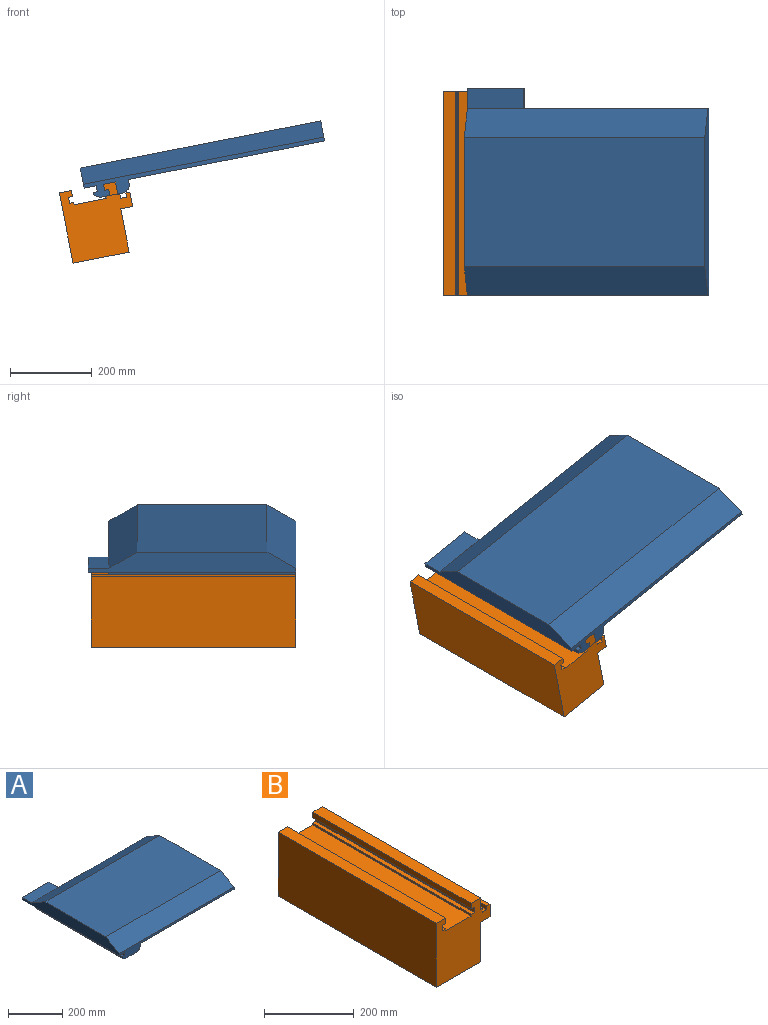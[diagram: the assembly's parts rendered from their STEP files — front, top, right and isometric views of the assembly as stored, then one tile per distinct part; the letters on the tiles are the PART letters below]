
ASSEMBLY  parts=2 mates=1
PART A: 19 faces, bbox 600x507.2x80 mm
  f0: plane 90x30mm, normal (0,1,0), area 2411.7mm2, adj f3,f4,f5,f6,f7,f8,f14,f15
  f1: plane 600x317.2mm, normal (0,0,1), area 190320mm2, adj f2,f9,f12,f13
  f2: plane 507.2x50mm, normal (-1,0,0), area 20505.5mm2, adj f1,f8,f10,f11,f12,f13,f16,f18
  f3: plane 457.2x15mm, normal (-1,0,0), area 6858mm2, adj f0,f4,f8,f10
  f4: plane 457.2x10mm, normal (0,0,1), area 4572mm2, adj f0,f3,f5,f10
  f5: plane 457.2x8.01mm, normal (-1,0,0), area 3660.1mm2, adj f0,f4,f10,f15
  f6: plane 457.2x55mm, normal (0,0,-1), area 25146mm2, adj f0,f10,f14,f15
  f7: plane 457.2x10mm, normal (1,0,0), area 4572mm2, adj f0,f8,f10,f14
  f8: plane 600x507.2mm, normal (0,0,-1), area 244744mm2, adj f0,f2,f3,f7,f9,f10,f11,f17
  f9: plane 457.2x50mm, normal (1,0,0), area 20031mm2, adj f1,f8,f10,f11,f12,f13
  f10: plane 600x39.59mm, normal (0,-1,0), area 8163mm2, adj f2,f3,f4,f5,f6,f7,f8,f9
  f11: plane 600x9.59mm, normal (0,1,0), area 4422.7mm2, adj f2,f8,f9,f13,f16,f17
  f12: plane 600x70mm, normal (0,-0.5,0.87), area 48497.4mm2, adj f1,f2,f9,f10
  f13: plane 600x70mm, normal (0,0.5,0.87), area 48497.4mm2, adj f1,f2,f9,f11
  f14: cylinder r=20mm len=457.2mm, axis (0,1,0), area 14363.4mm2, adj f0,f6,f7,f10
  f15: plane 457.2x15mm, normal (-0.42,0,-0.91), area 7567mm2, adj f0,f5,f6,f10
  f16: plane 140x50mm, normal (0,0,1), area 7000mm2, adj f2,f11,f17,f18
  f17: plane 50x9.49mm, normal (1,0,0), area 474.5mm2, adj f8,f11,f16,f18
  f18: plane 140x9.49mm, normal (0,1,0), area 1328.6mm2, adj f2,f8,f16,f17
PART B: 26 faces, bbox 170x500x175 mm
  f0: plane 500x30mm, normal (0,0,1), area 15000mm2, adj f1,f23,f24,f25
  f1: plane 500x175mm, normal (-1,0,0), area 87500mm2, adj f0,f2,f24,f25
  f2: plane 500x140mm, normal (0,0,-1), area 70000mm2, adj f1,f3,f24,f25
  f3: plane 500x108mm, normal (1,0,0), area 54000mm2, adj f2,f4,f24,f25
  f4: plane 500x30mm, normal (0,0,-1), area 15000mm2, adj f3,f5,f24,f25
  f5: plane 500x35mm, normal (1,0,0), area 17500mm2, adj f4,f6,f24,f25
  f6: plane 500x10mm, normal (0,0,1), area 5000mm2, adj f5,f7,f24,f25
  f7: plane 500x10mm, normal (-1,0,0), area 5000mm2, adj f6,f8,f24,f25
  f8: plane 500x15mm, normal (0,0,1), area 7500mm2, adj f7,f9,f24,f25
  f9: plane 500x10mm, normal (1,0,0), area 5000mm2, adj f8,f10,f24,f25
  f10: plane 500x5mm, normal (0,0,1), area 2500mm2, adj f9,f11,f24,f25
  f11: plane 500x32mm, normal (1,0,0), area 16000mm2, adj f10,f12,f24,f25
  f12: plane 500x30mm, normal (0,0,1), area 15000mm2, adj f11,f13,f24,f25
  f13: plane 500x15mm, normal (-1,0,0), area 7500mm2, adj f12,f14,f24,f25
  f14: plane 500x10mm, normal (0,0,-1), area 5000mm2, adj f13,f15,f24,f25
  f15: plane 500x15mm, normal (-1,0,0), area 7500mm2, adj f14,f16,f24,f25
  f16: plane 500x10mm, normal (0,0,1), area 5000mm2, adj f15,f17,f24,f25
  f17: plane 500x5mm, normal (-1,0,0), area 2500mm2, adj f16,f18,f24,f25
  f18: plane 500x80mm, normal (0,0,1), area 40000mm2, adj f17,f19,f24,f25
  f19: plane 500x5mm, normal (1,0,0), area 2500mm2, adj f18,f20,f24,f25
  f20: plane 500x10mm, normal (0,0,1), area 5000mm2, adj f19,f21,f24,f25
  f21: plane 500x15mm, normal (1,0,0), area 7500mm2, adj f20,f22,f24,f25
  f22: plane 500x10mm, normal (0,0,-1), area 5000mm2, adj f21,f23,f24,f25
  f23: plane 500x15mm, normal (1,0,0), area 7500mm2, adj f0,f22,f24,f25
  f24: plane 175x170mm, normal (0,1,0), area 22300mm2, adj f0,f1,f2,f3,f4,f5,f6,f7
  f25: plane 175x170mm, normal (0,-1,0), area 22300mm2, adj f0,f1,f2,f3,f4,f5,f6,f7
PLACE A rot(axis=(0,-1,0),11.1deg) t=(264.81,528.6,51.35)mm
PLACE B rot(axis=(0,-1,0),11.1deg) t=(78.51,71.4,-44.53)mm
MATE pin_slot A.f8 <-> B.f0  axis (0.19,0,-0.98) through (75.8,71.4,49.76)mm
